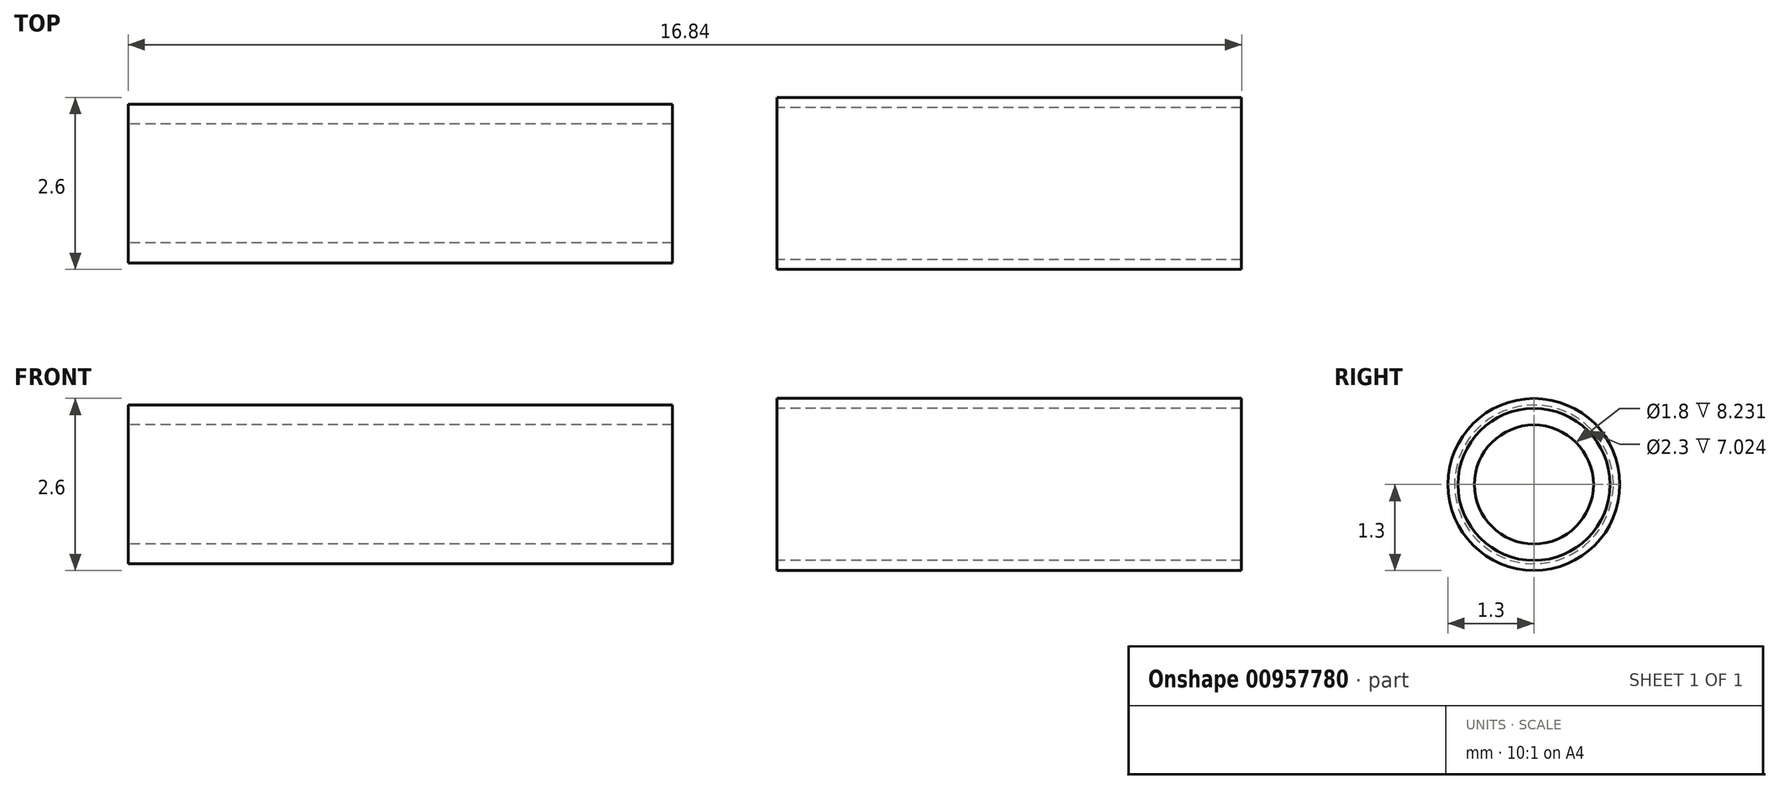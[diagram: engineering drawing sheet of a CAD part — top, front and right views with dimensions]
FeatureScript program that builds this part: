
annotation { "Feature Type Name" : "Feature", "Feature Type Description" : "" }
export const myFeature = defineFeature(function(context is Context, id is Id, definition is map)
    precondition{}
    {
        {
            var Q0;
            Q0=qCreatedBy(makeId("Top.planeOp"),FACE);
            var sketch = newSketch(context, id + "F0", { "sketchPlane" : qUnion([Q0])});
            skLineSegment(sketch, "E0", {"start": v(-9.25, 0) * mm, "end": v(8.42, 0) * mm, "construction": true});
            skLineSegment(sketch, "E1", {"start": v(-8.44, 1.2) * mm, "end": v(-8.44, 0.9) * mm});
            skLineSegment(sketch, "E2", {"start": v(-8.44, 0.9) * mm, "end": v(-0.2, 0.9) * mm});
            skLineSegment(sketch, "E3", {"start": v(-8.44, 1.2) * mm, "end": v(-0.2, 1.2) * mm});
            skLineSegment(sketch, "E4", {"start": v(-0.2, 1.2) * mm, "end": v(-0.2, 0.9) * mm});
            skPoint(sketch, "E5.firstSnap0", {"position": v(-0.2, 1.15) * mm});
            skLineSegment(sketch, "E5.bottom", {"start": v(1.37, 1.15) * mm, "end": v(8.4, 1.15) * mm});
            skLineSegment(sketch, "E5.top", {"start": v(1.37, 1.3) * mm, "end": v(8.4, 1.3) * mm});
            skLineSegment(sketch, "E5.left", {"start": v(1.37, 1.15) * mm, "end": v(1.37, 1.3) * mm});
            skLineSegment(sketch, "E5.right", {"start": v(8.4, 1.15) * mm, "end": v(8.4, 1.3) * mm});
            skSolve(sketch);
        }
        {
            var Q0;
            Q0 = qSketchRegion(id + "F0", true);
            var Q1;
            Q1=sQuery(id+"F0.wireOp",EDGE,"E0");
            revolve(context, id + "F1", {"surfaceOperationType" : NewSurfaceOperationType.NEW, "entities" : qUnion([Q0]), "axis" : qUnion([Q1]), "revolveType" : RevolveType.FULL});
        }
    });
